# Revit family: M5NX-E_2014
name_source: partatom
category: Specialty Equipment
revit_build: Autodesk Revit 2014 (Build: 20130308_1515(x64)
units: mm (PartAtom-declared; Revit-internal decimal feet)

## types (2) — shared parameters
Back Clearance = 3"
Bumper = Extruded PVC - 715 Cherry
Case = Textured Sheet Metal (Steel Painted) - 149 White Satin Matte
Case Interior - Back Panel = Sheet Metal (Steel Painted) - 700 Interior White
Case Interior - Side Panel = Mirror
Clearance = Yes
Cutsheet URL = www.hussmann.com/en/Technical%20Documents/0480115_G_M5NX-E.pdf
Depth = 37"
Description = 5 Deck Meat Merchandiser
End Weight = 100.00 lbf
Ends = Textured Sheet Metal (Steel Painted) - 149 White Satin Matte
Height = 78 3/8"
Manufacturer = Hussmann Corporation
Manufacturer Disclaimer = The information in this file is not intended to be an exact representation of the corresponding Hussmann product.  Further, we reserve the right to change or revise specifications and product design in connection with any feature of our products. Such changes do not entitle the buyer to corresponding changes, improvements, additions, or replacements for equipment previously sold or shipped.
Model = M5NX-E
Model URL = www.hussmann.com/en/product%20viewer/display-cases/M5X
Note from Manufacturer = This model only comes in 8'-0" and 12'-0" lengths.
Number of Shelves = 4
Refrig. Liquid = Liquid
Refrig. Suction = Suction
Refrigeration Lines Liquid = 3/8"
Refrigeration Lines Suction = 7/8"
Revit Family Date = 07/24/2015
Shelf = Yes
Shelves = Sheet Metal (Steel Painted) - 700 Interior White
Splashguard = Textured Sheet Metal (Steel Painted) - 701 Black
Top Clearance = 3"
Type Comments = Excel
URL = www.hussmann.com
Waste Drain = 1 1/4"

## per-type parameters (varying)
| type | Case Weight | Number of Supports | Total Weight | Width |
| 12'-0" Length | 1500.00 lbf | 4 | 1700.00 lbf | 144 1/2" |
| 8'-0" Length | 1100.00 lbf | 3 | 1300.00 lbf | 96 3/8" |

## geometry (parser evidence)
native form markers: Sweep x12
no freeform markers — native parametric forms only
